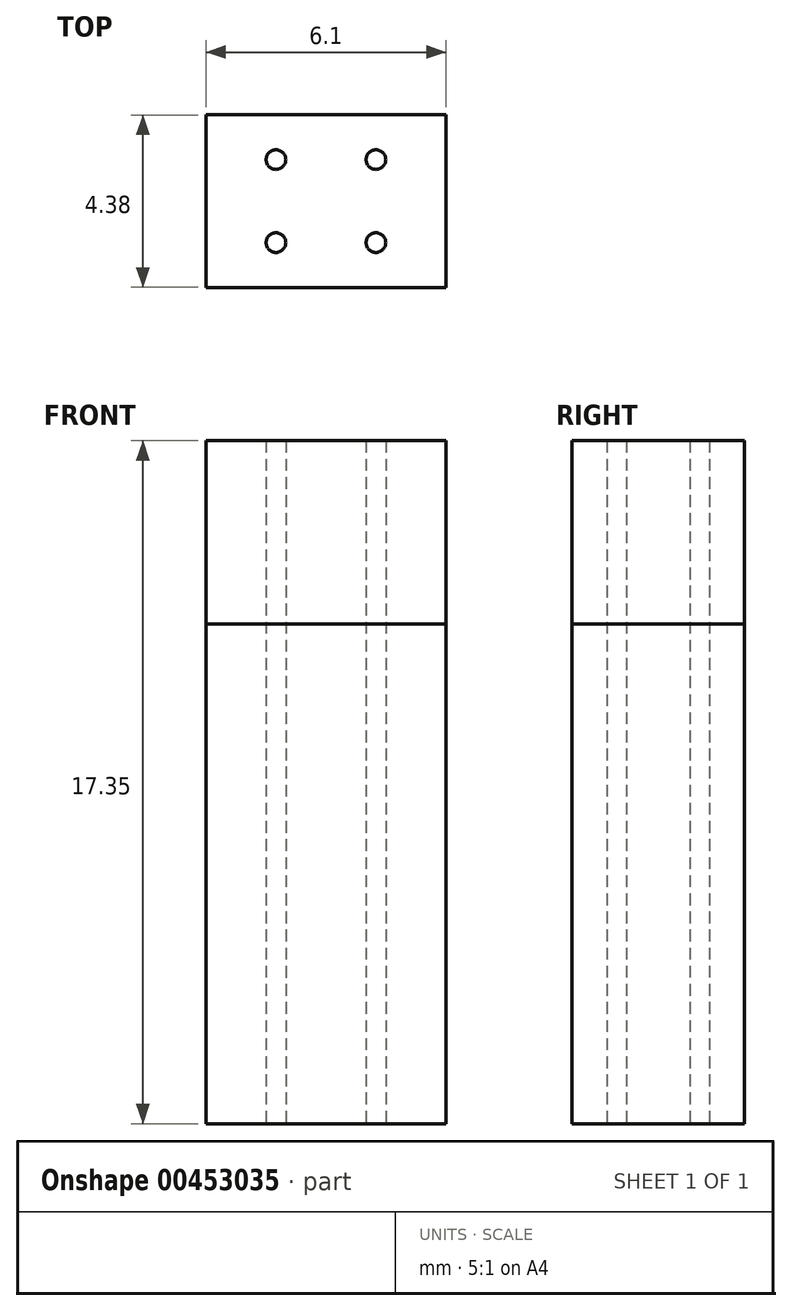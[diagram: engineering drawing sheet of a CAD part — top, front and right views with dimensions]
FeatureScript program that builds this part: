
annotation { "Feature Type Name" : "Feature", "Feature Type Description" : "" }
export const myFeature = defineFeature(function(context is Context, id is Id, definition is map)
    precondition{}
    {
        {
            var Q0;
            Q0=qCreatedBy(makeId("Top.planeOp"),FACE);
            var sketch = newSketch(context, id + "F0", { "sketchPlane" : qUnion([Q0])});
            skLineSegment(sketch, "E0", {"start": v(0, 11.55) * mm, "end": v(0, -11.98) * mm, "construction": true});
            skLineSegment(sketch, "E1", {"start": v(-17.25, 0) * mm, "end": v(13.8, 0) * mm, "construction": true});
            skLineSegment(sketch, "E2.bottom", {"start": v(3.05, 2.2) * mm, "end": v(-3.05, 2.2) * mm});
            skLineSegment(sketch, "E2.top", {"start": v(3.05, -2.2) * mm, "end": v(-3.05, -2.2) * mm});
            skLineSegment(sketch, "E2.left", {"start": v(3.05, 2.2) * mm, "end": v(3.05, -2.2) * mm});
            skLineSegment(sketch, "E2.right", {"start": v(-3.05, 2.2) * mm, "end": v(-3.05, -2.2) * mm});
            skPoint(sketch, "E2.middle", {"position": v(0, 0) * mm});
            skCircle(sketch, "E3", {"center": v(1.27, -1.05) * mm, "radius": 0.25 * mm});
            skCircle(sketch, "E4.MirrorC", {"center": v(-1.27, -1.05) * mm, "radius": 0.25 * mm});
            skCircle(sketch, "E5.MirrorC", {"center": v(-1.27, 1.05) * mm, "radius": 0.25 * mm});
            skCircle(sketch, "E6.MirrorC", {"center": v(1.27, 1.05) * mm, "radius": 0.25 * mm});
            skSolve(sketch);
        }
        {
            var Q0;
            Q0=makeQuery(id+"F0.imprint","IMPRINT",FACE,{"disambiguationData":[TD([[makeQuery(id+"F0.imprint","IMPRINT",EDGE,{"derivedFrom":sQuery(id+"F0.wireOp",EDGE,"E2.bottom")}),1.0]])]});
            extrude(context, id + "F1", {"entities" : qUnion([Q0]), "depth" : 4.65 * mm});
        }
        {
            var Q0;
            Q0=makeQuery(id+"F0.imprint","IMPRINT",FACE,{"disambiguationData":[TD([[makeQuery(id+"F0.imprint","IMPRINT",EDGE,{"derivedFrom":sQuery(id+"F0.wireOp",EDGE,"E6.MirrorC")}),-1.0]])]});
            var Q1;
            Q1=makeQuery(id+"F0.imprint","IMPRINT",FACE,{"disambiguationData":[TD([[makeQuery(id+"F0.imprint","IMPRINT",EDGE,{"derivedFrom":sQuery(id+"F0.wireOp",EDGE,"E5.MirrorC")}),1.0]])]});
            var Q2;
            Q2=makeQuery(id+"F0.imprint","IMPRINT",FACE,{"disambiguationData":[TD([[makeQuery(id+"F0.imprint","IMPRINT",EDGE,{"derivedFrom":sQuery(id+"F0.wireOp",EDGE,"E3")}),1.0]])]});
            var Q3;
            Q3=makeQuery(id+"F0.imprint","IMPRINT",FACE,{"disambiguationData":[TD([[makeQuery(id+"F0.imprint","IMPRINT",EDGE,{"derivedFrom":sQuery(id+"F0.wireOp",EDGE,"E4.MirrorC")}),-1.0]])]});
            extrude(context, id + "F2", {"entities" : qUnion([Q0, Q1, Q2, Q3]), "depth" : 4.65 * mm, "hasSecondDirection" : true, "secondDirectionOppositeDirection" : true, "secondDirectionDepth" : 12.7 * mm});
        }
    });
